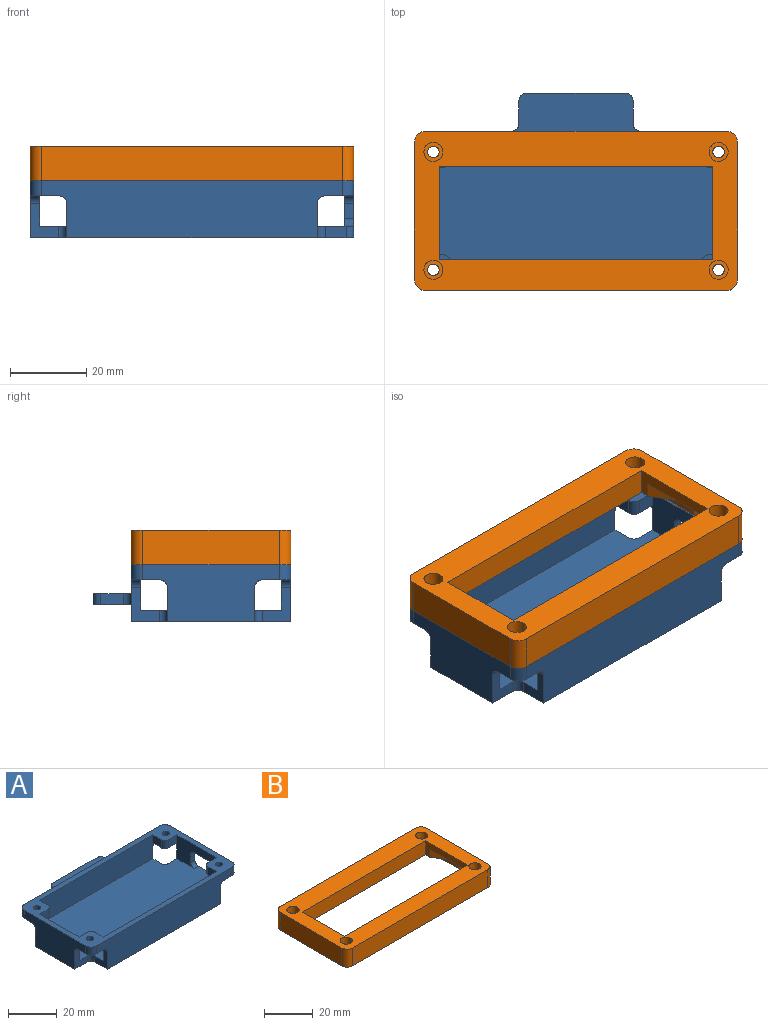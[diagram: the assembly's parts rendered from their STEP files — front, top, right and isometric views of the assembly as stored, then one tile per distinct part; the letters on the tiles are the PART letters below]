
ASSEMBLY  parts=2 mates=1
PART A: 67 faces, bbox 85x52x15 mm
  f0: plane 25x12mm, normal (-1,0,0), area 158.6mm2, adj f23,f24,f27,f29,f38,f39,f42,f47
  f1: plane 5.5x3mm, normal (0,-1,0), area 16.5mm2, adj f5,f23,f37,f57
  f2: plane 36x15mm, normal (-1,0,0), area 398.7mm2, adj f5,f13,f24,f30,f32,f35,f43,f46
  f3: plane 36x15mm, normal (1,0,0), area 273.6mm2, adj f5,f12,f23,f24,f31,f38,f39,f42
  f4: plane 79x15mm, normal (0,1,0), area 941.7mm2, adj f5,f12,f13,f24,f41,f42,f44,f46
  f5: plane 85x42mm, normal (0,0,-1), area 3211.6mm2, adj f1,f2,f3,f4,f25,f32,f33,f34
  f6: cylinder r=2mm len=4mm, axis (0,0,1), area 12.6mm2, adj f7,f24,f26,f46
  f7: plane 5x4mm, normal (1,0,0), area 20mm2, adj f6,f21,f24,f46
  f8: plane 5x4mm, normal (-1,0,0), area 20mm2, adj f9,f21,f24,f42
  f9: cylinder r=2mm len=4mm, axis (0,0,1), area 12.6mm2, adj f8,f24,f27,f42
  f10: cylinder r=1.5mm len=4mm, axis (0,0,1), area 37.7mm2, adj f24,f46
  f11: cylinder r=1.5mm len=4mm, axis (0,0,1), area 37.7mm2, adj f24,f42
  f12: cylinder r=3mm len=4mm, axis (0,0,1), area 18.8mm2, adj f3,f4,f24,f42
  f13: cylinder r=3mm len=4mm, axis (0,0,-1), area 18.8mm2, adj f2,f4,f24,f46
  f14: plane 5x4mm, normal (1,0,0), area 20mm2, adj f15,f20,f24,f35
  f15: cylinder r=2mm len=4mm, axis (0,0,1), area 12.6mm2, adj f14,f24,f28,f35
  f16: cylinder r=2mm len=4mm, axis (0,0,1), area 12.6mm2, adj f17,f24,f29,f38
  f17: plane 5x4mm, normal (-1,0,0), area 20mm2, adj f16,f20,f24,f38
  f18: cylinder r=1.5mm len=4mm, axis (0,0,1), area 37.7mm2, adj f24,f38
  f19: cylinder r=1.5mm len=4mm, axis (0,0,1), area 37.7mm2, adj f24,f35
  f20: plane 70x12mm, normal (0,1,0), area 793.7mm2, adj f14,f17,f23,f24,f33,f35,f36,f38
  f21: plane 70x12mm, normal (0,-1,0), area 793.7mm2, adj f7,f8,f23,f24,f41,f42,f44,f46
  f22: plane 27x12mm, normal (1,0,0), area 277.7mm2, adj f23,f24,f26,f28,f32,f35,f43,f46
  f23: plane 82.5x37mm, normal (0,0,1), area 2799.1mm2, adj f0,f1,f3,f20,f21,f22,f32,f33
  f24: plane 85x42mm, normal (0,0,1), area 766.6mm2, adj f0,f2,f3,f4,f6,f7,f8,f9
  f25: plane 79x15mm, normal (0,-1,0), area 1043.7mm2, adj f5,f24,f30,f31,f33,f35,f36,f38
  f26: plane 5x4mm, normal (0,-1,0), area 20mm2, adj f6,f22,f24,f46
  f27: plane 5x4mm, normal (0,-1,0), area 20mm2, adj f0,f9,f24,f42
  f28: plane 5x4mm, normal (0,1,0), area 20mm2, adj f15,f22,f24,f35
  f29: plane 5x4mm, normal (0,1,0), area 20mm2, adj f0,f16,f24,f38
  f30: cylinder r=3mm len=4mm, axis (0,0,1), area 18.8mm2, adj f2,f24,f25,f35
  f31: cylinder r=3mm len=4mm, axis (0,0,-1), area 18.8mm2, adj f3,f24,f25,f38
  f32: plane 9x7.5mm, normal (0,-1,0), area 37.5mm2, adj f2,f5,f22,f23,f34,f54
  f33: plane 9x7.5mm, normal (-1,0,0), area 37.5mm2, adj f5,f20,f23,f25,f34,f56
  f34: cylinder r=2mm len=3mm, axis (0,0,-1), area 9.4mm2, adj f5,f23,f32,f33
  f35: plane 9.5x9.5mm, normal (0,0,-1), area 70.4mm2, adj f2,f14,f15,f19,f20,f22,f25,f28
  f36: plane 9x7.5mm, normal (1,0,0), area 37.5mm2, adj f5,f20,f23,f25,f37,f55
  f37: cylinder r=2mm len=3mm, axis (0,0,-1), area 9.4mm2, adj f1,f5,f23,f36
  f38: plane 22.5x9.5mm, normal (0,0,-1), area 107.9mm2, adj f0,f3,f16,f17,f18,f20,f25,f29
  f39: plane 9x7.5mm, normal (0,1,0), area 37.5mm2, adj f0,f3,f5,f23,f40,f50
  f40: cylinder r=2mm len=3mm, axis (0,0,-1), area 9.4mm2, adj f5,f23,f39,f41
  f41: plane 9x7.5mm, normal (1,0,0), area 37.5mm2, adj f4,f5,f21,f23,f40,f52
  f42: plane 9.5x9.5mm, normal (0,0,-1), area 70.4mm2, adj f0,f3,f4,f8,f9,f11,f12,f21
  f43: plane 9x7.5mm, normal (0,1,0), area 37.5mm2, adj f2,f5,f22,f23,f45,f51
  f44: plane 9x7.5mm, normal (-1,0,0), area 37.5mm2, adj f4,f5,f21,f23,f45,f53
  f45: cylinder r=2mm len=3mm, axis (0,0,-1), area 9.4mm2, adj f5,f23,f43,f44
  f46: plane 9.5x9.5mm, normal (0,0,-1), area 70.4mm2, adj f2,f4,f6,f7,f10,f13,f21,f22
  f47: plane 4x2.5mm, normal (0,-1,0), area 10mm2, adj f0,f3,f48,f49
  f48: cylinder r=2mm len=2.5mm, axis (-1,0,0), area 7.9mm2, adj f0,f3,f23,f47
  f49: cylinder r=2mm len=2.5mm, axis (-1,0,0), area 7.9mm2, adj f0,f3,f38,f47
  f50: cylinder r=2mm len=2.5mm, axis (-1,0,0), area 7.9mm2, adj f0,f3,f39,f42
  f51: cylinder r=2mm len=2.5mm, axis (-1,0,0), area 7.9mm2, adj f2,f22,f43,f46
  f52: cylinder r=2mm len=2.5mm, axis (0,1,0), area 7.9mm2, adj f4,f21,f41,f42
  f53: cylinder r=2mm len=2.5mm, axis (0,-1,0), area 7.9mm2, adj f4,f21,f44,f46
  f54: cylinder r=2mm len=2.5mm, axis (1,0,0), area 7.9mm2, adj f2,f22,f32,f35
  f55: cylinder r=2mm len=2.5mm, axis (0,1,0), area 7.9mm2, adj f20,f25,f36,f38
  f56: cylinder r=2mm len=2.5mm, axis (0,-1,0), area 7.9mm2, adj f20,f25,f33,f35
  f57: cylinder r=2mm len=3mm, axis (0,0,-1), area 9.4mm2, adj f1,f3,f5,f23
  f58: plane 34x10mm, normal (0,0,-1), area 300mm2, adj f4,f59,f61,f62,f63,f64,f65,f66
  f59: plane 6x3mm, normal (-1,0,0), area 18mm2, adj f58,f60,f63,f65
  f60: plane 34x10mm, normal (0,0,1), area 300mm2, adj f4,f59,f61,f62,f63,f64,f65,f66
  f61: plane 6x3mm, normal (1,0,0), area 18mm2, adj f58,f60,f64,f66
  f62: plane 26x3mm, normal (0,1,0), area 78mm2, adj f58,f60,f65,f66
  f63: cylinder r=2mm len=3mm, axis (0,0,1), area 9.4mm2, adj f4,f58,f59,f60
  f64: cylinder r=2mm len=3mm, axis (0,0,-1), area 9.4mm2, adj f4,f58,f60,f61
  f65: cylinder r=2mm len=3mm, axis (0,0,-1), area 9.4mm2, adj f58,f59,f60,f62
  f66: cylinder r=2mm len=3mm, axis (0,0,1), area 9.4mm2, adj f58,f60,f61,f62
PART B: 40 faces, bbox 85x42x9 mm
  f0: cylinder r=1.5mm len=3mm, axis (0,0,1), area 28.3mm2, adj f4,f29
  f1: cylinder r=1.5mm len=3mm, axis (0,0,1), area 28.3mm2, adj f4,f27
  f2: cylinder r=1.5mm len=3mm, axis (0,0,1), area 28.3mm2, adj f4,f25
  f3: cylinder r=1.5mm len=3mm, axis (0,0,1), area 28.3mm2, adj f4,f23
  f4: plane 81x37mm, normal (0,0,-1), area 965.8mm2, adj f0,f1,f2,f3,f10,f11,f12,f13
  f5: plane 85x42mm, normal (0,0,1), area 1719.7mm2, adj f6,f7,f8,f9,f10,f11,f12,f13
  f6: plane 79x9mm, normal (0,-1,0), area 711mm2, adj f5,f31,f34,f39
  f7: plane 36x9mm, normal (1,0,0), area 324mm2, adj f5,f31,f32,f39
  f8: plane 79x9mm, normal (0,1,0), area 711mm2, adj f5,f32,f33,f39
  f9: plane 36x9mm, normal (-1,0,0), area 324mm2, adj f5,f33,f34,f39
  f10: plane 72x7mm, normal (0,1,0), area 504mm2, adj f4,f5,f11,f13
  f11: plane 24.5x7mm, normal (-1,0,0), area 93.3mm2, adj f4,f5,f10,f12,f14,f16,f17
  f12: plane 72x7mm, normal (0,-1,0), area 504mm2, adj f4,f5,f11,f13
  f13: plane 24.5x7mm, normal (1,0,0), area 171.5mm2, adj f4,f5,f10,f12
  f14: plane 7.28x4.15mm, normal (-0.87,-0.49,0), area 33.5mm2, adj f4,f11,f15,f17
  f15: plane 5x4mm, normal (-1,0,0), area 20mm2, adj f4,f14,f16,f17
  f16: plane 7.28x4.15mm, normal (-0.87,0.49,0), area 33.5mm2, adj f4,f11,f15,f17
  f17: plane 19.56x4.15mm, normal (0,0,-1), area 50.9mm2, adj f11,f14,f15,f16
  f18: plane 47x4mm, normal (0,1,0), area 188mm2, adj f4,f19,f21,f22
  f19: plane 4x4mm, normal (1,0,0), area 16mm2, adj f4,f18,f20,f22
  f20: plane 47x4mm, normal (0,-1,0), area 188mm2, adj f4,f19,f21,f22
  f21: plane 4x4mm, normal (-1,0,0), area 16mm2, adj f4,f18,f20,f22
  f22: plane 47x4mm, normal (0,0,-1), area 188mm2, adj f18,f19,f20,f21
  f23: plane 5x5mm, normal (0,0,1), area 12.6mm2, adj f3,f24
  f24: cylinder r=2.5mm len=5mm, axis (0,0,1), area 62.8mm2, adj f5,f23
  f25: plane 5x5mm, normal (0,0,1), area 12.6mm2, adj f2,f26
  f26: cylinder r=2.5mm len=5mm, axis (0,0,1), area 62.8mm2, adj f5,f25
  f27: plane 5x5mm, normal (0,0,1), area 12.6mm2, adj f1,f28
  f28: cylinder r=2.5mm len=5mm, axis (0,0,1), area 62.8mm2, adj f5,f27
  f29: plane 5x5mm, normal (0,0,1), area 12.6mm2, adj f0,f30
  f30: cylinder r=2.5mm len=5mm, axis (0,0,1), area 62.8mm2, adj f5,f29
  f31: cylinder r=3mm len=9mm, axis (0,0,1), area 42.4mm2, adj f5,f6,f7,f39
  f32: cylinder r=3mm len=9mm, axis (0,0,-1), area 42.4mm2, adj f5,f7,f8,f39
  f33: cylinder r=3mm len=9mm, axis (0,0,1), area 42.4mm2, adj f5,f8,f9,f39
  f34: cylinder r=3mm len=9mm, axis (0,0,-1), area 42.4mm2, adj f5,f6,f9,f39
  f35: plane 81x2mm, normal (0,-1,0), area 162mm2, adj f4,f36,f38,f39
  f36: plane 37x2mm, normal (1,0,0), area 74mm2, adj f4,f35,f37,f39
  f37: plane 81x2mm, normal (0,1,0), area 162mm2, adj f4,f36,f38,f39
  f38: plane 37x2mm, normal (-1,0,0), area 74mm2, adj f4,f35,f37,f39
  f39: plane 85x42mm, normal (0,0,-1), area 565.3mm2, adj f6,f7,f8,f9,f31,f32,f33,f34
PLACE A t=(-29.24,-17.9,-21.46)mm
PLACE B t=(-29.24,-17.9,-4.46)mm
MATE fastened A.f19 <-> B.f3  axis (0,0,1) through (-66.74,-33.4,-6.46)mm
